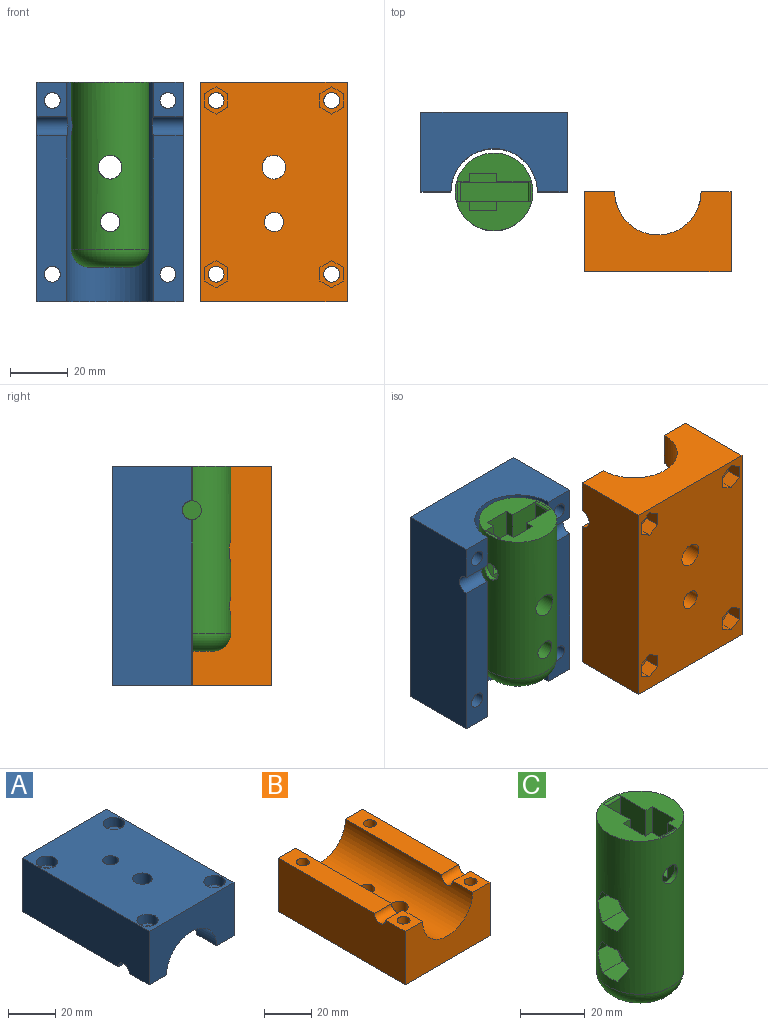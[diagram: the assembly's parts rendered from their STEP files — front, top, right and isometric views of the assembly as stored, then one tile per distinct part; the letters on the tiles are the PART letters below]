
ASSEMBLY  parts=3 mates=4
PART A: 26 faces, bbox 50.8x76.2x27.7 mm
  f0: cylinder r=2.75mm len=22.86mm, axis (0,0,1), area 395mm2, adj f11,f24
  f1: cylinder r=2.75mm len=22.86mm, axis (0,0,1), area 395mm2, adj f9,f23
  f2: cylinder r=2.75mm len=22.86mm, axis (0,0,1), area 395mm2, adj f5,f21
  f3: cylinder r=2.75mm len=22.86mm, axis (0,0,1), area 395mm2, adj f6,f18
  f4: plane 76.2x50.8mm, normal (0,0,1), area 3527.4mm2, adj f7,f8,f12,f13,f16,f17,f19,f20
  f5: plane 57.59x10.4mm, normal (0,0,-1), area 575.1mm2, adj f2,f8,f10,f13,f15
  f6: plane 57.59x10.4mm, normal (0,0,-1), area 575.1mm2, adj f3,f7,f10,f13,f14
  f7: plane 76.2x27.69mm, normal (1,0,0), area 2091.8mm2, adj f4,f6,f11,f12,f13,f14
  f8: plane 76.2x27.69mm, normal (-1,0,0), area 2091.8mm2, adj f4,f5,f9,f12,f13,f15
  f9: plane 11.87x10.4mm, normal (0,0,-1), area 99.7mm2, adj f1,f8,f10,f12,f15
  f10: cylinder r=15mm len=76.2mm, axis (0,1,0), area 3465.1mm2, adj f5,f6,f9,f11,f12,f13,f14,f15
  f11: plane 11.87x10.4mm, normal (0,0,-1), area 99.7mm2, adj f0,f7,f10,f12,f14
  f12: plane 50.8x27.69mm, normal (0,-1,0), area 1053mm2, adj f4,f7,f8,f9,f10,f11
  f13: plane 50.8x27.69mm, normal (0,1,0), area 1053mm2, adj f4,f5,f6,f7,f8,f10
  f14: cylinder r=3.37mm len=10.78mm, axis (1,0,0), area 112.2mm2, adj f6,f7,f10,f11
  f15: cylinder r=3.37mm len=10.78mm, axis (1,0,0), area 112.2mm2, adj f5,f8,f9,f10
  f16: cylinder r=3.37mm len=13.07mm, axis (0,0,1), area 272.3mm2, adj f4,f10
  f17: cylinder r=4.13mm len=13.27mm, axis (0,0,1), area 336.5mm2, adj f4,f10
  f18: plane 9x9mm, normal (0,0,1), area 39.9mm2, adj f3,f19
  f19: cylinder r=4.5mm len=9mm, axis (0,0,1), area 136.5mm2, adj f4,f18
  f20: cylinder r=4.5mm len=9mm, axis (0,0,1), area 136.5mm2, adj f4,f21
  f21: plane 9x9mm, normal (0,0,1), area 39.9mm2, adj f2,f20
  f22: cylinder r=4.5mm len=9mm, axis (0,0,1), area 136.5mm2, adj f4,f23
  f23: plane 9x9mm, normal (0,0,1), area 39.9mm2, adj f1,f22
  f24: plane 9x9mm, normal (0,0,1), area 39.9mm2, adj f0,f25
  f25: cylinder r=4.5mm len=9mm, axis (0,0,1), area 136.5mm2, adj f4,f24
PART B: 46 faces, bbox 50.8x76.2x27.7 mm
  f0: plane 76.2x50.8mm, normal (0,0,-1), area 3548.9mm2, adj f7,f8,f12,f13,f16,f17,f18,f19
  f1: cylinder r=2.75mm len=22.19mm, axis (0,0,1), area 383.3mm2, adj f11,f39
  f2: cylinder r=2.75mm len=22.19mm, axis (0,0,1), area 383.3mm2, adj f9,f38
  f3: cylinder r=2.75mm len=22.19mm, axis (0,0,1), area 383.3mm2, adj f6,f25
  f4: cylinder r=2.75mm len=22.19mm, axis (0,0,1), area 383.3mm2, adj f5,f24
  f5: plane 11.87x10.4mm, normal (0,0,1), area 99.7mm2, adj f4,f8,f10,f12,f15
  f6: plane 11.87x10.4mm, normal (0,0,1), area 99.7mm2, adj f3,f7,f10,f12,f14
  f7: plane 76.2x27.69mm, normal (1,0,0), area 2091.8mm2, adj f0,f6,f11,f12,f13,f14
  f8: plane 76.2x27.69mm, normal (-1,0,0), area 2091.8mm2, adj f0,f5,f9,f12,f13,f15
  f9: plane 57.59x10.4mm, normal (0,0,1), area 575.1mm2, adj f2,f8,f10,f13,f15
  f10: cylinder r=15mm len=76.2mm, axis (0,1,0), area 3464.9mm2, adj f5,f6,f9,f11,f12,f13,f14,f15
  f11: plane 57.59x10.4mm, normal (0,0,1), area 575.1mm2, adj f1,f7,f10,f13,f14
  f12: plane 50.8x27.69mm, normal (0,-1,0), area 1053mm2, adj f0,f5,f6,f7,f8,f10
  f13: plane 50.8x27.69mm, normal (0,1,0), area 1053mm2, adj f0,f7,f8,f9,f10,f11
  f14: cylinder r=3.37mm len=10.78mm, axis (1,0,0), area 112.2mm2, adj f6,f7,f10,f11
  f15: cylinder r=3.37mm len=10.78mm, axis (1,0,0), area 112.2mm2, adj f5,f8,f9,f10
  f16: cylinder r=3.37mm len=13.07mm, axis (0,0,1), area 272.3mm2, adj f0,f10
  f17: cylinder r=4.13mm len=13.27mm, axis (0,0,1), area 336.5mm2, adj f0,f10
  f18: plane 5.5x4.73mm, normal (-1,0,0), area 26mm2, adj f0,f19,f23,f24
  f19: plane 5.5x4.1mm, normal (-0.5,0.87,0), area 26mm2, adj f0,f18,f20,f24
  f20: plane 5.5x4.1mm, normal (0.5,0.87,0), area 26mm2, adj f0,f19,f21,f24
  f21: plane 5.5x4.73mm, normal (1,0,0), area 26mm2, adj f0,f20,f22,f24
  f22: plane 5.5x4.1mm, normal (0.5,-0.87,0), area 26mm2, adj f0,f21,f23,f24
  f23: plane 5.5x4.1mm, normal (-0.5,-0.87,0), area 26mm2, adj f0,f18,f22,f24
  f24: plane 9.47x8.2mm, normal (0,0,-1), area 34.5mm2, adj f4,f18,f19,f20,f21,f22,f23
  f25: plane 9.47x8.2mm, normal (0,0,-1), area 34.5mm2, adj f3,f26,f27,f28,f29,f30,f31
  f26: plane 5.5x4.73mm, normal (1,0,0), area 26mm2, adj f0,f25,f27,f31
  f27: plane 5.5x4.1mm, normal (0.5,-0.87,0), area 26mm2, adj f0,f25,f26,f28
  f28: plane 5.5x4.1mm, normal (-0.5,-0.87,0), area 26mm2, adj f0,f25,f27,f29
  f29: plane 5.5x4.73mm, normal (-1,0,0), area 26mm2, adj f0,f25,f28,f30
  f30: plane 5.5x4.1mm, normal (-0.5,0.87,0), area 26mm2, adj f0,f25,f29,f31
  f31: plane 5.5x4.1mm, normal (0.5,0.87,0), area 26mm2, adj f0,f25,f26,f30
  f32: plane 5.5x4.73mm, normal (-1,0,0), area 26mm2, adj f0,f33,f37,f38
  f33: plane 5.5x4.1mm, normal (-0.5,0.87,0), area 26mm2, adj f0,f32,f34,f38
  f34: plane 5.5x4.1mm, normal (0.5,0.87,0), area 26mm2, adj f0,f33,f35,f38
  f35: plane 5.5x4.73mm, normal (1,0,0), area 26mm2, adj f0,f34,f36,f38
  f36: plane 5.5x4.1mm, normal (0.5,-0.87,0), area 26mm2, adj f0,f35,f37,f38
  f37: plane 5.5x4.1mm, normal (-0.5,-0.87,0), area 26mm2, adj f0,f32,f36,f38
  f38: plane 9.47x8.2mm, normal (0,0,-1), area 34.5mm2, adj f2,f32,f33,f34,f35,f36,f37
  f39: plane 9.47x8.2mm, normal (0,0,-1), area 34.5mm2, adj f1,f40,f41,f42,f43,f44,f45
  f40: plane 5.5x4.73mm, normal (-1,0,0), area 26mm2, adj f0,f39,f41,f45
  f41: plane 5.5x4.1mm, normal (-0.5,0.87,0), area 26mm2, adj f0,f39,f40,f42
  f42: plane 5.5x4.1mm, normal (0.5,0.87,0), area 26mm2, adj f0,f39,f41,f43
  f43: plane 5.5x4.73mm, normal (1,0,0), area 26mm2, adj f0,f39,f42,f44
  f44: plane 5.5x4.1mm, normal (0.5,-0.87,0), area 26mm2, adj f0,f39,f43,f45
  f45: plane 5.5x4.1mm, normal (-0.5,-0.87,0), area 26mm2, adj f0,f39,f40,f44
PART C: 38 faces, bbox 29.2x29.2x64.3 mm
  f0: cylinder r=13.5mm len=57.91mm, axis (0,0,-1), area 4535.6mm2, adj f1,f8,f17,f18,f19,f22,f23,f24
  f1: plane 27x27mm, normal (0,0,1), area 342.9mm2, adj f0,f2,f3,f10,f11,f12,f13,f14
  f2: plane 59.18x25.2mm, normal (1,0,0), area 1111mm2, adj f1,f5,f6,f7,f13,f15,f16,f20
  f3: plane 59.18x25.2mm, normal (-1,0,0), area 1111mm2, adj f1,f5,f6,f7,f9,f10,f11,f18
  f4: plane 14.3x14.3mm, normal (0,0,-1), area 160.6mm2, adj f8
  f5: plane 58.39x6.86mm, normal (0,-1,0), area 400.5mm2, adj f2,f3,f7,f37
  f6: plane 58.39x6.86mm, normal (0,1,0), area 367mm2, adj f2,f3,f7,f17,f36
  f7: plane 23.62x6.86mm, normal (0,0,1), area 162mm2, adj f2,f3,f5,f6
  f8: torus R=7.15mm, axis (0,0,1), area 701.5mm2, adj f0,f4
  f9: plane 9.53x2.98mm, normal (0,0,1), area 28.4mm2, adj f3,f10,f11,f12
  f10: plane 20.8x2.98mm, normal (0,1,0), area 62.1mm2, adj f1,f3,f9,f12
  f11: plane 20.8x2.98mm, normal (0,-1,0), area 62.1mm2, adj f1,f3,f9,f12
  f12: plane 20.8x9.53mm, normal (-1,0,0), area 198.1mm2, adj f1,f9,f10,f11
  f13: plane 20.8x2.98mm, normal (0,-1,0), area 62.1mm2, adj f1,f2,f14,f16
  f14: plane 20.8x9.53mm, normal (1,0,0), area 198.1mm2, adj f1,f13,f15,f16
  f15: plane 20.8x2.98mm, normal (0,1,0), area 62.1mm2, adj f1,f2,f14,f16
  f16: plane 9.53x2.98mm, normal (0,0,1), area 28.4mm2, adj f2,f13,f14,f15
  f17: cylinder r=3.26mm len=6.53mm, axis (0,1,0), area 30.6mm2, adj f0,f6
  f18: cylinder r=3.37mm len=10.07mm, axis (-1,0,0), area 208.5mm2, adj f0,f3
  f19: cylinder r=4.13mm len=10.07mm, axis (-1,0,0), area 252.8mm2, adj f0,f3
  f20: cylinder r=3.37mm len=6.73mm, axis (1,0,0), area 18.8mm2, adj f2,f35
  f21: cylinder r=4.13mm len=8.26mm, axis (1,0,0), area 23.1mm2, adj f2,f28
  f22: plane 8.74x5.95mm, normal (0,-0.87,-0.5), area 55.8mm2, adj f0,f23,f27,f28
  f23: plane 9.18x6.87mm, normal (0,0,-1), area 62.1mm2, adj f0,f22,f24,f28
  f24: plane 8.74x5.95mm, normal (0,0.87,-0.5), area 55.8mm2, adj f0,f23,f25,f28
  f25: plane 8.74x5.95mm, normal (0,0.87,0.5), area 55.8mm2, adj f0,f24,f26,f28
  f26: plane 9.18x6.87mm, normal (0,0,1), area 62.1mm2, adj f0,f25,f27,f28
  f27: plane 8.74x5.95mm, normal (0,-0.87,0.5), area 55.8mm2, adj f0,f22,f26,f28
  f28: plane 13.75x11.91mm, normal (-1,0,0), area 69.2mm2, adj f21,f22,f23,f24,f25,f26,f27
  f29: plane 8.74x5.95mm, normal (0,-0.87,-0.5), area 55.8mm2, adj f0,f30,f34,f35
  f30: plane 9.18x6.87mm, normal (0,0,-1), area 62.1mm2, adj f0,f29,f31,f35
  f31: plane 8.74x5.95mm, normal (0,0.87,-0.5), area 55.8mm2, adj f0,f30,f32,f35
  f32: plane 8.74x5.95mm, normal (0,0.87,0.5), area 55.8mm2, adj f0,f31,f33,f35
  f33: plane 9.18x6.87mm, normal (0,0,1), area 62.1mm2, adj f0,f32,f34,f35
  f34: plane 8.74x5.95mm, normal (0,-0.87,0.5), area 55.8mm2, adj f0,f29,f33,f35
  f35: plane 13.75x11.91mm, normal (-1,0,0), area 87.2mm2, adj f20,f29,f30,f31,f32,f33,f34
  f36: cylinder r=0.79mm len=6.86mm, axis (-1,0,0), area 8.5mm2, adj f1,f2,f3,f6
  f37: cylinder r=0.79mm len=6.86mm, axis (1,0,0), area 8.5mm2, adj f1,f2,f3,f5
PLACE A rot(axis=(-1,0,0),90deg) t=(-54.72,15.63,-12.16)mm
PLACE B rot(axis=(-1,0,0),90deg) t=(2.17,15.63,-12.16)mm
PLACE C rot(axis=(0,0,-1),90deg) t=(-54.72,1.78,-0.22)mm
MATE cylindrical C.f17 <-> A.f14  axis (1,0,0) through (-66.54,1.78,48.8)mm
MATE cylindrical C.f19 <-> A.f17  axis (0,1,0) through (-54.72,-1.65,34.55)mm
MATE planar A.f12 <-> B.f12  axis (0,0,1) through (-54.72,29.47,64.04)mm
MATE planar B.f9 <-> A.f5  axis (0,1,0) through (-12.83,1.78,16.63)mm
